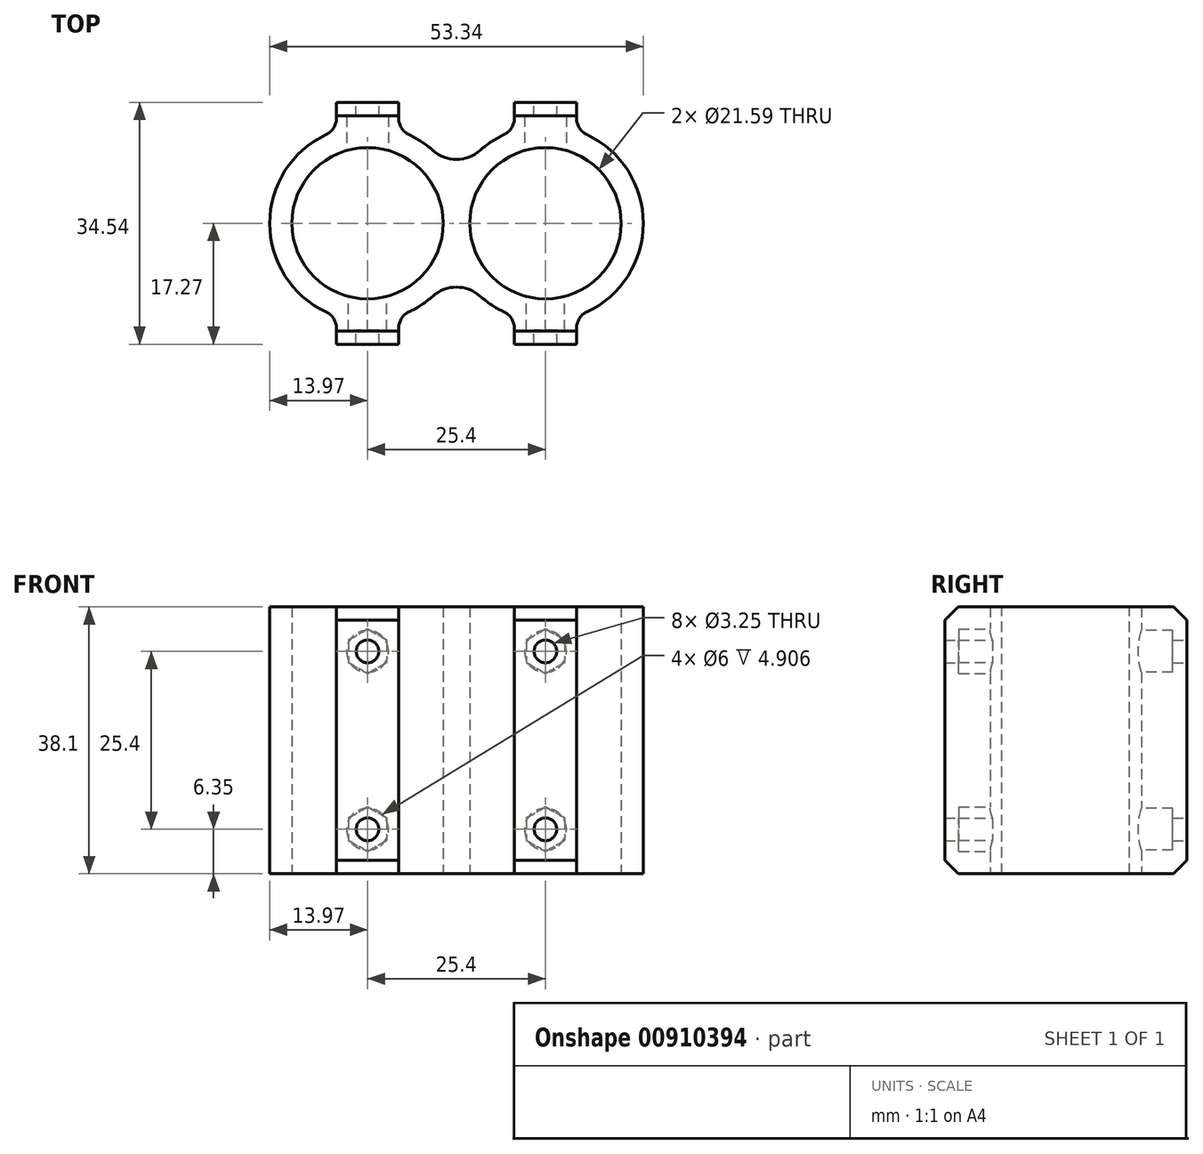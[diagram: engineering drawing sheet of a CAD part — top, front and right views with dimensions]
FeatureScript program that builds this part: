
annotation { "Feature Type Name" : "Feature", "Feature Type Description" : "" }
export const myFeature = defineFeature(function(context is Context, id is Id, definition is map)
    precondition{}
    {
        {
            var Q0;
            Q0=qCreatedBy(makeId("Top.planeOp"),FACE);
            var sketch = newSketch(context, id + "F0", { "sketchPlane" : qUnion([Q0])});
            skCircle(sketch, "E0", {"center": v(-12.7, 0) * mm, "radius": 10.8 * mm});
            skCircle(sketch, "E1", {"center": v(12.7, 0) * mm, "radius": 10.8 * mm});
            skLineSegment(sketch, "E2", {"start": v(-12.7, 0) * mm, "end": v(12.7, 0) * mm, "construction": true});
            skArc(sketch, "E3", {"start": v(0, 5.82) * mm, "mid": v(-3.36, 10.39) * mm, "end": v(-8.26, 13.24) * mm});
            skArc(sketch, "E4", {"start": v(0, -5.82) * mm, "mid": v(3.36, -10.39) * mm, "end": v(8.26, -13.24) * mm});
            skLineSegment(sketch, "E5.top", {"start": v(-17.15, 17.27) * mm, "end": v(-8.26, 17.27) * mm});
            skLineSegment(sketch, "E5.left", {"start": v(-17.15, 13.24) * mm, "end": v(-17.15, 17.27) * mm});
            skLineSegment(sketch, "E5.right", {"start": v(-8.26, 13.24) * mm, "end": v(-8.26, 17.27) * mm});
            skArc(sketch, "E6.trimOffspring", {"start": v(-17.15, 13.24) * mm, "mid": v(-26.67, 0) * mm, "end": v(-17.14, -13.24) * mm});
            skLineSegment(sketch, "E7", {"start": v(-15.5, 10.43) * mm, "end": v(-15.5, 15.3) * mm, "construction": true});
            skLineSegment(sketch, "E8", {"start": v(-15.5, 15.3) * mm, "end": v(-14.2, 15.3) * mm, "construction": true});
            skLineSegment(sketch, "E9", {"start": v(-14.2, 15.3) * mm, "end": v(-14.2, 17.27) * mm, "construction": true});
            skLineSegment(sketch, "E10", {"start": v(-12.7, 17.27) * mm, "end": v(-12.7, 10.8) * mm, "construction": true});
            skLineSegment(sketch, "E11", {"start": v(-17.14, -13.24) * mm, "end": v(-17.14, -17.27) * mm});
            skLineSegment(sketch, "E12", {"start": v(-17.14, -17.27) * mm, "end": v(-8.25, -17.27) * mm});
            skLineSegment(sketch, "E13", {"start": v(-8.25, -17.27) * mm, "end": v(-8.25, -13.24) * mm});
            skLineSegment(sketch, "E14", {"start": v(8.26, -13.24) * mm, "end": v(8.26, -17.27) * mm});
            skLineSegment(sketch, "E15", {"start": v(8.26, -17.27) * mm, "end": v(17.14, -17.27) * mm});
            skLineSegment(sketch, "E16", {"start": v(17.14, -17.27) * mm, "end": v(17.14, -13.24) * mm});
            skLineSegment(sketch, "E17", {"start": v(17.14, 13.24) * mm, "end": v(17.14, 17.27) * mm});
            skLineSegment(sketch, "E18", {"start": v(17.14, 17.27) * mm, "end": v(8.26, 17.27) * mm});
            skLineSegment(sketch, "E19", {"start": v(8.26, 17.27) * mm, "end": v(8.26, 13.24) * mm});
            skArc(sketch, "E20.trimOffspring", {"start": v(-8.25, -13.24) * mm, "mid": v(-3.36, -10.39) * mm, "end": v(0, -5.82) * mm});
            skArc(sketch, "E21.trimOffspring", {"start": v(17.14, -13.24) * mm, "mid": v(26.67, 0) * mm, "end": v(17.14, 13.24) * mm});
            skArc(sketch, "E22.trimOffspring", {"start": v(8.26, 13.24) * mm, "mid": v(3.36, 10.39) * mm, "end": v(0, 5.82) * mm});
            skSolve(sketch);
        }
        {
            var Q0;
            Q0 = qSketchRegion(id + "F0", true);
            extrude(context, id + "F1", {"entities" : qUnion([Q0]), "depth" : 38.1 * mm, "offsetDistance" : 25.4 * mm});
        }
        {
            var Q0;
            Q0=makeQuery(id+"F1.opExtrude","SWEPT_FACE",FACE,{"disambiguationData":[OSD([sQuery(id+"F0.wireOp",EDGE,"E12")])]});
            var sketch = newSketch(context, id + "F2", { "sketchPlane" : qUnion([Q0])});
            skLineSegment(sketch, "E23.bottom", {"start": v(12.7, 31.75) * mm, "end": v(-12.7, 31.75) * mm});
            skLineSegment(sketch, "E23.top", {"start": v(12.7, 6.35) * mm, "end": v(-12.7, 6.35) * mm});
            skLineSegment(sketch, "E23.left", {"start": v(12.7, 31.75) * mm, "end": v(12.7, 6.35) * mm});
            skLineSegment(sketch, "E23.right", {"start": v(-12.7, 31.75) * mm, "end": v(-12.7, 6.35) * mm});
            skPoint(sketch, "E23.middle", {"position": v(0, 19.05) * mm});
            skSolve(sketch);
        }
        {
            var Q0;
            Q0=sQuery(id+"F2.wireOp",VERTEX,"E23.bottom.end");
            var Q1;
            Q1=sQuery(id+"F2.wireOp",VERTEX,"E23.bottom.start");
            var Q2;
            Q2=sQuery(id+"F2.wireOp",VERTEX,"E23.top.start");
            var Q3;
            Q3=sQuery(id+"F2.wireOp",VERTEX,"E23.top.end");
            var Q4;
            Q4=makeQuery(id+"F1.opExtrude","SWEPT_BODY",BODY,{"disambiguationData":[OSD([sQuery(id+"F0.wireOp",EDGE,"E0"),sQuery(id+"F0.wireOp",EDGE,"E1"),sQuery(id+"F0.wireOp",EDGE,"E3"),sQuery(id+"F0.wireOp",EDGE,"E4"),sQuery(id+"F0.wireOp",EDGE,"E5.top"),sQuery(id+"F0.wireOp",EDGE,"E5.left"),sQuery(id+"F0.wireOp",EDGE,"E5.right"),sQuery(id+"F0.wireOp",EDGE,"E6.trimOffspring"),sQuery(id+"F0.wireOp",EDGE,"E11"),sQuery(id+"F0.wireOp",EDGE,"E12"),sQuery(id+"F0.wireOp",EDGE,"E13"),sQuery(id+"F0.wireOp",EDGE,"E14"),sQuery(id+"F0.wireOp",EDGE,"E15"),sQuery(id+"F0.wireOp",EDGE,"E16"),sQuery(id+"F0.wireOp",EDGE,"E17"),sQuery(id+"F0.wireOp",EDGE,"E18"),sQuery(id+"F0.wireOp",EDGE,"E19"),sQuery(id+"F0.wireOp",EDGE,"E20.trimOffspring"),sQuery(id+"F0.wireOp",EDGE,"E21.trimOffspring"),sQuery(id+"F0.wireOp",EDGE,"E22.trimOffspring")])]});
            hole(context, id + "F3", {"style" : HoleStyle.SIMPLE, "endStyle" : HoleEndStyle.THROUGH, "holeDiameter" : 3.25 * mm, "majorDiameter" : 6.35 * mm, "isTappedThrough" : true, "tappedDepth" : 12.7 * mm, "tapClearance" : 3, "locations" : qUnion([Q0, Q1, Q2, Q3]), "scope" : qUnion([Q4])});
        }
        {
            var Q0;
            Q0=qCreatedBy(makeId("Front.planeOp"),FACE);
            var sketch = newSketch(context, id + "F4", { "sketchPlane" : qUnion([Q0])});
            skCircle(sketch, "E24", {"center": v(-12.7, 31.75) * mm, "radius": 3 * mm});
            skCircle(sketch, "E25", {"center": v(-12.7, 6.35) * mm, "radius": 3 * mm});
            skCircle(sketch, "E26", {"center": v(12.7, 6.35) * mm, "radius": 3 * mm});
            skCircle(sketch, "E27", {"center": v(12.7, 31.75) * mm, "radius": 3 * mm});
            skSolve(sketch);
        }
        {
            var Q0;
            Q0 = qSketchRegion(id + "F4", true);
            var Q1;
            Q1=makeQuery(id+"F1.opExtrude","SWEPT_FACE",FACE,{"disambiguationData":[OSD([sQuery(id+"F0.wireOp",EDGE,"E18")])]});
            extrude(context, id + "F5", {"entities" : qUnion([Q0]), "operationType" : NewBodyOperationType.REMOVE, "endBound" : BoundingType.UP_TO_SURFACE, "oppositeDirection" : true, "depth" : 25.4 * mm, "endBoundEntityFace" : qUnion([Q1]), "hasOffset" : true, "offsetDistance" : 2 * mm});
        }
        {
            var Q0;
            Q0=qCreatedBy(makeId("Front.planeOp"),FACE);
            var sketch = newSketch(context, id + "F6", { "sketchPlane" : qUnion([Q0])});
            skCircle(sketch, "E28.cCircle", {"center": v(-12.7, 31.75) * mm, "radius": 2.74 * mm, "construction": true});
            skLineSegment(sketch, "E28.0", {"start": v(-9.96, 33.33) * mm, "end": v(-9.96, 30.17) * mm});
            skLineSegment(sketch, "E28.1", {"start": v(-9.96, 30.17) * mm, "end": v(-12.7, 28.58) * mm});
            skLineSegment(sketch, "E28.2", {"start": v(-12.7, 28.58) * mm, "end": v(-15.44, 30.17) * mm});
            skLineSegment(sketch, "E28.3", {"start": v(-15.44, 30.17) * mm, "end": v(-15.44, 33.33) * mm});
            skLineSegment(sketch, "E28.4", {"start": v(-15.44, 33.33) * mm, "end": v(-12.7, 34.92) * mm});
            skLineSegment(sketch, "E28.5", {"start": v(-12.7, 34.92) * mm, "end": v(-9.96, 33.33) * mm});
            skPoint(sketch, "E28.0.midPoint", {"position": v(-9.96, 31.75) * mm});
            skCircle(sketch, "E29.cCircle", {"center": v(-12.7, 6.35) * mm, "radius": 2.74 * mm, "construction": true});
            skLineSegment(sketch, "E29.0", {"start": v(-9.96, 7.93) * mm, "end": v(-9.96, 4.77) * mm});
            skLineSegment(sketch, "E29.1", {"start": v(-9.96, 4.77) * mm, "end": v(-12.7, 3.18) * mm});
            skLineSegment(sketch, "E29.2", {"start": v(-12.7, 3.18) * mm, "end": v(-15.44, 4.77) * mm});
            skLineSegment(sketch, "E29.3", {"start": v(-15.44, 4.77) * mm, "end": v(-15.44, 7.93) * mm});
            skLineSegment(sketch, "E29.4", {"start": v(-15.44, 7.93) * mm, "end": v(-12.7, 9.52) * mm});
            skLineSegment(sketch, "E29.5", {"start": v(-12.7, 9.52) * mm, "end": v(-9.96, 7.93) * mm});
            skPoint(sketch, "E29.0.midPoint", {"position": v(-9.96, 6.35) * mm});
            skCircle(sketch, "E30.cCircle", {"center": v(12.7, 6.35) * mm, "radius": 2.74 * mm, "construction": true});
            skLineSegment(sketch, "E30.0", {"start": v(15.44, 7.93) * mm, "end": v(15.44, 4.77) * mm});
            skLineSegment(sketch, "E30.1", {"start": v(15.44, 4.77) * mm, "end": v(12.7, 3.18) * mm});
            skLineSegment(sketch, "E30.2", {"start": v(12.7, 3.18) * mm, "end": v(9.96, 4.77) * mm});
            skLineSegment(sketch, "E30.3", {"start": v(9.96, 4.77) * mm, "end": v(9.96, 7.93) * mm});
            skLineSegment(sketch, "E30.4", {"start": v(9.96, 7.93) * mm, "end": v(12.7, 9.52) * mm});
            skLineSegment(sketch, "E30.5", {"start": v(12.7, 9.52) * mm, "end": v(15.44, 7.93) * mm});
            skPoint(sketch, "E30.0.midPoint", {"position": v(15.44, 6.35) * mm});
            skCircle(sketch, "E31.cCircle", {"center": v(12.7, 31.75) * mm, "radius": 2.74 * mm, "construction": true});
            skLineSegment(sketch, "E31.0", {"start": v(15.44, 33.33) * mm, "end": v(15.44, 30.17) * mm});
            skLineSegment(sketch, "E31.1", {"start": v(15.44, 30.17) * mm, "end": v(12.7, 28.58) * mm});
            skLineSegment(sketch, "E31.2", {"start": v(12.7, 28.58) * mm, "end": v(9.96, 30.17) * mm});
            skLineSegment(sketch, "E31.3", {"start": v(9.96, 30.17) * mm, "end": v(9.96, 33.33) * mm});
            skLineSegment(sketch, "E31.4", {"start": v(9.96, 33.33) * mm, "end": v(12.7, 34.92) * mm});
            skLineSegment(sketch, "E31.5", {"start": v(12.7, 34.92) * mm, "end": v(15.44, 33.33) * mm});
            skPoint(sketch, "E31.0.midPoint", {"position": v(15.44, 31.75) * mm});
            skSolve(sketch);
        }
        {
            var Q0;
            Q0 = qSketchRegion(id + "F6", true);
            var Q1;
            Q1=makeQuery(id+"F1.opExtrude","SWEPT_FACE",FACE,{"disambiguationData":[OSD([sQuery(id+"F0.wireOp",EDGE,"E12")])]});
            extrude(context, id + "F7", {"entities" : qUnion([Q0]), "operationType" : NewBodyOperationType.REMOVE, "endBound" : BoundingType.UP_TO_SURFACE, "depth" : 25.4 * mm, "endBoundEntityFace" : qUnion([Q1]), "hasOffset" : true, "offsetDistance" : 2 * mm});
        }
        {
            var Q0;
            Q0=makeQuery(id+"F1.opExtrude","CAP_EDGE",EDGE,{"disambiguationData":[OSD([sQuery(id+"F0.wireOp",EDGE,"E15")])],"isStart":false});
            var Q1;
            Q1=makeQuery(id+"F1.opExtrude","CAP_EDGE",EDGE,{"disambiguationData":[OSD([sQuery(id+"F0.wireOp",EDGE,"E15")])],"isStart":true});
            var Q2;
            Q2=makeQuery(id+"F1.opExtrude","CAP_EDGE",EDGE,{"disambiguationData":[OSD([sQuery(id+"F0.wireOp",EDGE,"E12")])],"isStart":true});
            var Q3;
            Q3=makeQuery(id+"F1.opExtrude","CAP_EDGE",EDGE,{"disambiguationData":[OSD([sQuery(id+"F0.wireOp",EDGE,"E12")])],"isStart":false});
            var Q4;
            Q4=makeQuery(id+"F1.opExtrude","CAP_EDGE",EDGE,{"disambiguationData":[OSD([sQuery(id+"F0.wireOp",EDGE,"E18")])],"isStart":false});
            var Q5;
            Q5=makeQuery(id+"F1.opExtrude","CAP_EDGE",EDGE,{"disambiguationData":[OSD([sQuery(id+"F0.wireOp",EDGE,"E18")])],"isStart":true});
            var Q6;
            Q6=makeQuery(id+"F1.opExtrude","CAP_EDGE",EDGE,{"disambiguationData":[OSD([sQuery(id+"F0.wireOp",EDGE,"E5.top")])],"isStart":true});
            var Q7;
            Q7=makeQuery(id+"F1.opExtrude","CAP_EDGE",EDGE,{"disambiguationData":[OSD([sQuery(id+"F0.wireOp",EDGE,"E5.top")])],"isStart":false});
            chamfer(context, id + "F8", {"entities" : qUnion([Q0, Q1, Q2, Q3, Q4, Q5, Q6, Q7]), "width" : 1.9 * mm, "tangentPropagation" : true});
        }
        {
            var Q0;
            Q0=makeQuery(id+"F1.opExtrude","SWEPT_EDGE",EDGE,{"disambiguationData":[OSD([sQuery(id+"F0.wireOp",EDGE,"E3"),sQuery(id+"F0.wireOp",EDGE,"E22.trimOffspring")])]});
            var Q1;
            Q1=makeQuery(id+"F1.opExtrude","SWEPT_EDGE",EDGE,{"disambiguationData":[OSD([sQuery(id+"F0.wireOp",EDGE,"E4"),sQuery(id+"F0.wireOp",EDGE,"E20.trimOffspring")])]});
            fillet(context, id + "F9", {"entities" : qUnion([Q0, Q1]), "radius" : 5.08 * mm, "tangentPropagation" : true, "allowEdgeOverflow" : false});
        }
        {
            var Q0;
            Q0=makeQuery(id+"F1.opExtrude","SWEPT_EDGE",EDGE,{"disambiguationData":[OSD([sQuery(id+"F0.wireOp",EDGE,"E13"),sQuery(id+"F0.wireOp",EDGE,"E20.trimOffspring")])]});
            var Q1;
            Q1=makeQuery(id+"F1.opExtrude","SWEPT_EDGE",EDGE,{"disambiguationData":[OSD([sQuery(id+"F0.wireOp",EDGE,"E4"),sQuery(id+"F0.wireOp",EDGE,"E14")])]});
            var Q2;
            Q2=makeQuery(id+"F1.opExtrude","SWEPT_EDGE",EDGE,{"disambiguationData":[OSD([sQuery(id+"F0.wireOp",EDGE,"E16"),sQuery(id+"F0.wireOp",EDGE,"E21.trimOffspring")])]});
            var Q3;
            Q3=makeQuery(id+"F1.opExtrude","SWEPT_EDGE",EDGE,{"disambiguationData":[OSD([sQuery(id+"F0.wireOp",EDGE,"E17"),sQuery(id+"F0.wireOp",EDGE,"E21.trimOffspring")])]});
            var Q4;
            Q4=makeQuery(id+"F1.opExtrude","SWEPT_EDGE",EDGE,{"disambiguationData":[OSD([sQuery(id+"F0.wireOp",EDGE,"E19"),sQuery(id+"F0.wireOp",EDGE,"E22.trimOffspring")])]});
            var Q5;
            Q5=makeQuery(id+"F1.opExtrude","SWEPT_EDGE",EDGE,{"disambiguationData":[OSD([sQuery(id+"F0.wireOp",EDGE,"E5.left"),sQuery(id+"F0.wireOp",EDGE,"E6.trimOffspring")])]});
            var Q6;
            Q6=makeQuery(id+"F1.opExtrude","SWEPT_EDGE",EDGE,{"disambiguationData":[OSD([sQuery(id+"F0.wireOp",EDGE,"E3"),sQuery(id+"F0.wireOp",EDGE,"E5.right")])]});
            var Q7;
            Q7=makeQuery(id+"F1.opExtrude","SWEPT_EDGE",EDGE,{"disambiguationData":[OSD([sQuery(id+"F0.wireOp",EDGE,"E6.trimOffspring"),sQuery(id+"F0.wireOp",EDGE,"E11")])]});
            fillet(context, id + "F10", {"entities" : qUnion([Q0, Q1, Q2, Q3, Q4, Q5, Q6, Q7]), "radius" : 2.54 * mm, "tangentPropagation" : true, "allowEdgeOverflow" : false});
        }
    });
